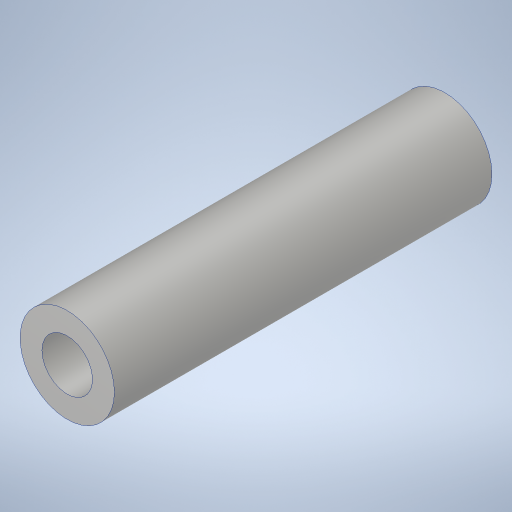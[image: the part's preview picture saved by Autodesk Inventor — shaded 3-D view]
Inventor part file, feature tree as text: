
AUTODESK INVENTOR PART (.ipt)
format: ipt  version: 2023.4 (Build 274418000, 418)  size: 241,664 bytes
history: native  units: in
note: dims shown in document units (in); Inventor stores cm internally (conversion verified against a paired STEP export)
features: extrude x1, hole x1
ambient origin geometry x8: Origin, YZ Plane, XZ Plane, XY Plane, X Axis, Y Axis, Z Axis, Center Point
bodies: Solid1 (feature_tree)
feature tree (2):
  extrude  "Extrusion1"  Depth=1.5in
  hole  "Hole1"  [1 undecoded]
note: 1 required parameter value undecoded (feature->parameter linkage not recoverable at this tier; creation-order binding heuristic only, values carry confidence <= 0.55)
